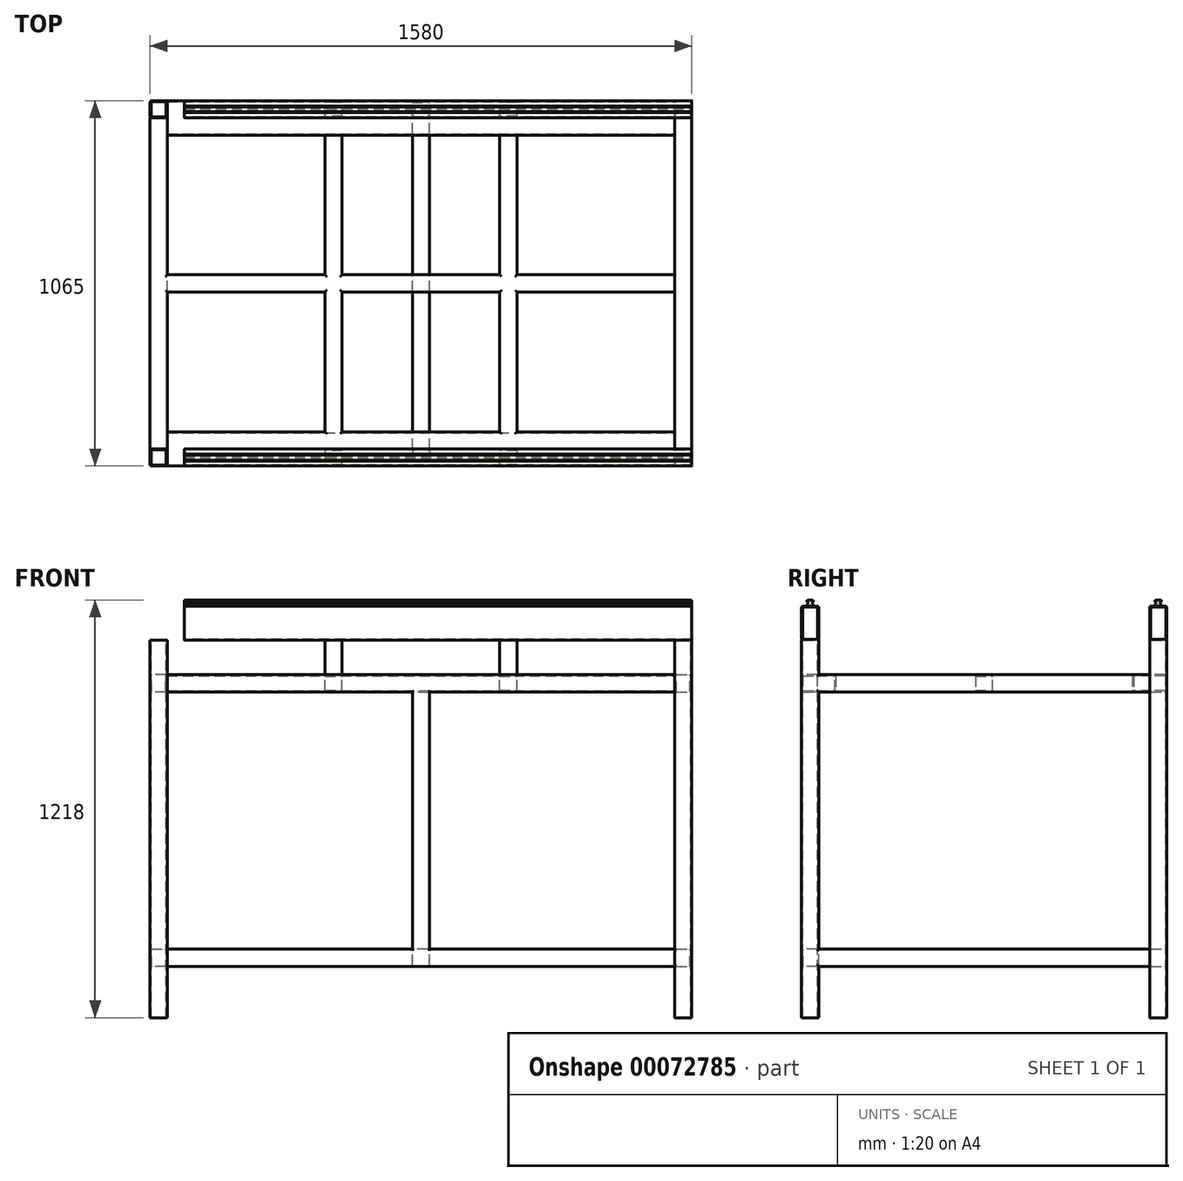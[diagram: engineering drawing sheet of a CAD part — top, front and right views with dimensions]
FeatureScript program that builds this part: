
annotation { "Feature Type Name" : "Feature", "Feature Type Description" : "" }
export const myFeature = defineFeature(function(context is Context, id is Id, definition is map)
    precondition{}
    {
        {
            var Q0;
            Q0=qCreatedBy(makeId("Right.planeOp"),FACE);
            var sketch = newSketch(context, id + "F0", { "sketchPlane" : qUnion([Q0])});
            skLineSegment(sketch, "E0.rect.bottom", {"start": v(20, 50) * mm, "end": v(-20, 50) * mm});
            skLineSegment(sketch, "E0.rect.top", {"start": v(20, -50) * mm, "end": v(-20, -50) * mm});
            skLineSegment(sketch, "E0.rect.left", {"start": v(25, 45) * mm, "end": v(25, -45) * mm});
            skLineSegment(sketch, "E0.rect.right", {"start": v(-25, 45) * mm, "end": v(-25, -45) * mm});
            skPoint(sketch, "E0.rect.middle", {"position": v(0, 0) * mm});
            skPoint(sketch, "E1.visualSharp", {"position": v(-25, 50) * mm});
            skArc(sketch, "E1.filletArc", {"start": v(-20, 50) * mm, "mid": v(-23.54, 48.54) * mm, "end": v(-25, 45) * mm});
            skPoint(sketch, "E2.visualSharp", {"position": v(25, 50) * mm});
            skArc(sketch, "E2.filletArc", {"start": v(25, 45) * mm, "mid": v(23.54, 48.54) * mm, "end": v(20, 50) * mm});
            skPoint(sketch, "E3.visualSharp", {"position": v(25, -50) * mm});
            skArc(sketch, "E3.filletArc", {"start": v(20, -50) * mm, "mid": v(23.54, -48.54) * mm, "end": v(25, -45) * mm});
            skPoint(sketch, "E4.visualSharp", {"position": v(-25, -50) * mm});
            skArc(sketch, "E4.filletArc", {"start": v(-25, -45) * mm, "mid": v(-23.54, -48.54) * mm, "end": v(-20, -50) * mm});
            skLineSegment(sketch, "E5.0", {"start": v(-22, 47) * mm, "end": v(-22, -47) * mm});
            skLineSegment(sketch, "E5.1", {"start": v(22, 47) * mm, "end": v(-22, 47) * mm});
            skLineSegment(sketch, "E5.2", {"start": v(22, 47) * mm, "end": v(22, -47) * mm});
            skLineSegment(sketch, "E5.3", {"start": v(22, -47) * mm, "end": v(-22, -47) * mm});
            skSolve(sketch);
        }
        {
            var Q0;
            Q0=qCreatedBy(makeId("Right.planeOp"),FACE);
            var sketch = newSketch(context, id + "F1", { "sketchPlane" : qUnion([Q0])});
            skLineSegment(sketch, "E6.rect.bottom", {"start": v(-995, 50) * mm, "end": v(-1035, 50) * mm});
            skLineSegment(sketch, "E6.rect.top", {"start": v(-995, -50) * mm, "end": v(-1035, -50) * mm});
            skLineSegment(sketch, "E6.rect.left", {"start": v(-990, 45) * mm, "end": v(-990, -45) * mm});
            skLineSegment(sketch, "E6.rect.right", {"start": v(-1040, 45) * mm, "end": v(-1040, -45) * mm});
            skPoint(sketch, "E6.rect.middle", {"position": v(0, 0) * mm});
            skPoint(sketch, "E7.visualSharp", {"position": v(-1040, 50) * mm});
            skArc(sketch, "E7.filletArc", {"start": v(-1035, 50) * mm, "mid": v(-1038.54, 48.54) * mm, "end": v(-1040, 45) * mm});
            skPoint(sketch, "E8.visualSharp", {"position": v(-990, 50) * mm});
            skArc(sketch, "E8.filletArc", {"start": v(-990, 45) * mm, "mid": v(-991.46, 48.54) * mm, "end": v(-995, 50) * mm});
            skPoint(sketch, "E9.visualSharp", {"position": v(-990, -50) * mm});
            skArc(sketch, "E9.filletArc", {"start": v(-995, -50) * mm, "mid": v(-991.46, -48.54) * mm, "end": v(-990, -45) * mm});
            skPoint(sketch, "E10.visualSharp", {"position": v(-1040, -50) * mm});
            skArc(sketch, "E10.filletArc", {"start": v(-1040, -45) * mm, "mid": v(-1038.54, -48.54) * mm, "end": v(-1035, -50) * mm});
            skLineSegment(sketch, "E11.0", {"start": v(-1037, 47) * mm, "end": v(-1037, -47) * mm});
            skLineSegment(sketch, "E11.1", {"start": v(-993, 47) * mm, "end": v(-1037, 47) * mm});
            skLineSegment(sketch, "E11.2", {"start": v(-993, 47) * mm, "end": v(-993, -47) * mm});
            skLineSegment(sketch, "E11.3", {"start": v(-993, -47) * mm, "end": v(-1037, -47) * mm});
            skSolve(sketch);
        }
        {
            var Q0;
            Q0=makeQuery(id+"F1.imprint","IMPRINT",FACE,{"disambiguationData":[TD([[makeQuery(id+"F1.imprint","IMPRINT",EDGE,{"derivedFrom":sQuery(id+"F1.wireOp",EDGE,"E6.rect.bottom")}),1.0]])]});
            var Q1;
            Q1=makeQuery(id+"F0.imprint","IMPRINT",FACE,{"disambiguationData":[TD([[makeQuery(id+"F0.imprint","IMPRINT",EDGE,{"derivedFrom":sQuery(id+"F0.wireOp",EDGE,"E0.rect.bottom")}),1.0]])]});
            extrude(context, id + "F2", {"entities" : qUnion([Q0, Q1]), "depth" : 1480 * mm});
        }
        {
            var Q0;
            Q0=makeQuery(id+"F2.opExtrude","CAP_FACE",FACE,{"disambiguationData":[OSD([sQuery(id+"F1.wireOp",EDGE,"E6.rect.bottom"),sQuery(id+"F1.wireOp",EDGE,"E6.rect.top"),sQuery(id+"F1.wireOp",EDGE,"E6.rect.left"),sQuery(id+"F1.wireOp",EDGE,"E6.rect.right"),sQuery(id+"F1.wireOp",EDGE,"E7.filletArc"),sQuery(id+"F1.wireOp",EDGE,"E8.filletArc"),sQuery(id+"F1.wireOp",EDGE,"E9.filletArc"),sQuery(id+"F1.wireOp",EDGE,"E10.filletArc"),sQuery(id+"F1.wireOp",EDGE,"E11.0"),sQuery(id+"F1.wireOp",EDGE,"E11.1"),sQuery(id+"F1.wireOp",EDGE,"E11.2"),sQuery(id+"F1.wireOp",EDGE,"E11.3")])],"isStart":false});
            cPlane(context, id + "F3", {"entities" : qUnion([Q0]), "cplaneType" : CPlaneType.OFFSET, "offset" : 50 * mm, "oppositeDirection" : true, "width" : 150 * mm, "height" : 150 * mm});
        }
        {
            var Q0;
            Q0=qCreatedBy(id+"F3.planeOp",FACE);
            var sketch = newSketch(context, id + "F4", { "sketchPlane" : qUnion([Q0])});
            skLineSegment(sketch, "E12.bottom", {"start": v(-1035, -150) * mm, "end": v(-945, -150) * mm});
            skLineSegment(sketch, "E12.top", {"start": v(-1035, -200) * mm, "end": v(-945, -200) * mm});
            skLineSegment(sketch, "E12.left", {"start": v(-1040, -155) * mm, "end": v(-1040, -195) * mm});
            skLineSegment(sketch, "E12.right", {"start": v(-940, -155) * mm, "end": v(-940, -195) * mm});
            skPoint(sketch, "E13.visualSharp", {"position": v(-1040, -150) * mm});
            skArc(sketch, "E13.filletArc", {"start": v(-1035, -150) * mm, "mid": v(-1038.54, -151.46) * mm, "end": v(-1040, -155) * mm});
            skPoint(sketch, "E14.visualSharp", {"position": v(-940, -150) * mm});
            skArc(sketch, "E14.filletArc", {"start": v(-940, -155) * mm, "mid": v(-941.46, -151.46) * mm, "end": v(-945, -150) * mm});
            skPoint(sketch, "E15.visualSharp", {"position": v(-940, -200) * mm});
            skArc(sketch, "E15.filletArc", {"start": v(-945, -200) * mm, "mid": v(-941.46, -198.54) * mm, "end": v(-940, -195) * mm});
            skPoint(sketch, "E16.visualSharp", {"position": v(-1040, -200) * mm});
            skArc(sketch, "E16.filletArc", {"start": v(-1040, -195) * mm, "mid": v(-1038.54, -198.54) * mm, "end": v(-1035, -200) * mm});
            skLineSegment(sketch, "E17.0", {"start": v(-995, -50) * mm, "end": v(-1035, -50) * mm});
            skLineSegment(sketch, "E18.0", {"start": v(-1040, 45) * mm, "end": v(-1040, -45) * mm});
            skLineSegment(sketch, "E19.0", {"start": v(-943, -153) * mm, "end": v(-943, -197) * mm});
            skLineSegment(sketch, "E19.1", {"start": v(-1037, -153) * mm, "end": v(-943, -153) * mm});
            skLineSegment(sketch, "E19.2", {"start": v(-1037, -153) * mm, "end": v(-1037, -197) * mm});
            skLineSegment(sketch, "E19.3", {"start": v(-1037, -197) * mm, "end": v(-943, -197) * mm});
            skLineSegment(sketch, "E20.bottom", {"start": v(20, -150) * mm, "end": v(-70, -150) * mm});
            skLineSegment(sketch, "E20.top", {"start": v(20, -200) * mm, "end": v(-70, -200) * mm});
            skLineSegment(sketch, "E20.left", {"start": v(25, -155) * mm, "end": v(25, -195) * mm});
            skLineSegment(sketch, "E20.right", {"start": v(-75, -155) * mm, "end": v(-75, -195) * mm});
            skPoint(sketch, "E21.0", {"position": v(25, -50) * mm});
            skPoint(sketch, "E22.visualSharp", {"position": v(-75, -150) * mm});
            skArc(sketch, "E22.filletArc", {"start": v(-70, -150) * mm, "mid": v(-73.54, -151.46) * mm, "end": v(-75, -155) * mm});
            skPoint(sketch, "E23.visualSharp", {"position": v(25, -200) * mm});
            skArc(sketch, "E23.filletArc", {"start": v(20, -200) * mm, "mid": v(23.54, -198.54) * mm, "end": v(25, -195) * mm});
            skPoint(sketch, "E24.visualSharp", {"position": v(25, -150) * mm});
            skArc(sketch, "E24.filletArc", {"start": v(25, -155) * mm, "mid": v(23.54, -151.46) * mm, "end": v(20, -150) * mm});
            skPoint(sketch, "E25.visualSharp", {"position": v(-75, -200) * mm});
            skArc(sketch, "E25.filletArc", {"start": v(-75, -195) * mm, "mid": v(-73.54, -198.54) * mm, "end": v(-70, -200) * mm});
            skLineSegment(sketch, "E26.0", {"start": v(22, -153) * mm, "end": v(-72, -153) * mm});
            skLineSegment(sketch, "E26.1", {"start": v(22, -153) * mm, "end": v(22, -197) * mm});
            skLineSegment(sketch, "E26.2", {"start": v(22, -197) * mm, "end": v(-72, -197) * mm});
            skLineSegment(sketch, "E26.3", {"start": v(-72, -153) * mm, "end": v(-72, -197) * mm});
            skSolve(sketch);
        }
        {
            var Q0;
            Q0=makeQuery(id+"F4.imprint","IMPRINT",FACE,{"disambiguationData":[TD([[makeQuery(id+"F4.imprint","IMPRINT",EDGE,{"derivedFrom":sQuery(id+"F4.wireOp",EDGE,"E12.bottom")}),-1.0]])]});
            var Q1;
            Q1=makeQuery(id+"F4.imprint","IMPRINT",FACE,{"disambiguationData":[TD([[makeQuery(id+"F4.imprint","IMPRINT",EDGE,{"derivedFrom":sQuery(id+"F4.wireOp",EDGE,"E20.bottom")}),1.0]])]});
            extrude(context, id + "F5", {"entities" : qUnion([Q0, Q1]), "oppositeDirection" : true, "depth" : 1480 * mm});
        }
        {
            var Q0;
            Q0=makeQuery(id+"F2.opExtrude","SWEPT_FACE",FACE,{"disambiguationData":[OSD([sQuery(id+"F1.wireOp",EDGE,"E6.rect.top")])]});
            cPlane(context, id + "F6", {"entities" : qUnion([Q0]), "cplaneType" : CPlaneType.OFFSET, "offset" : 0 * mm, "width" : 150 * mm, "height" : 150 * mm});
        }
        {
            var Q0;
            Q0=qCreatedBy(id+"F6.planeOp",FACE);
            var sketch = newSketch(context, id + "F7", { "sketchPlane" : qUnion([Q0])});
            skPoint(sketch, "E27.0", {"position": v(1480, 990) * mm});
            skPoint(sketch, "E28.0", {"position": v(1430, 1040) * mm});
            skLineSegment(sketch, "E29.bottom", {"start": v(1435, 1040) * mm, "end": v(1475, 1040) * mm});
            skLineSegment(sketch, "E29.top", {"start": v(1435, 990) * mm, "end": v(1475, 990) * mm});
            skLineSegment(sketch, "E29.left", {"start": v(1430, 1035) * mm, "end": v(1430, 995) * mm});
            skLineSegment(sketch, "E29.right", {"start": v(1480, 1035) * mm, "end": v(1480, 995) * mm});
            skPoint(sketch, "E30.visualSharp", {"position": v(1480, 1040) * mm});
            skArc(sketch, "E30.filletArc", {"start": v(1480, 1035) * mm, "mid": v(1478.54, 1038.54) * mm, "end": v(1475, 1040) * mm});
            skArc(sketch, "E31.filletArc", {"start": v(1475, 990) * mm, "mid": v(1478.54, 991.46) * mm, "end": v(1480, 995) * mm});
            skPoint(sketch, "E32.visualSharp", {"position": v(1430, 990) * mm});
            skArc(sketch, "E32.filletArc", {"start": v(1430, 995) * mm, "mid": v(1431.46, 991.46) * mm, "end": v(1435, 990) * mm});
            skArc(sketch, "E33.filletArc", {"start": v(1435, 1040) * mm, "mid": v(1431.46, 1038.54) * mm, "end": v(1430, 1035) * mm});
            skLineSegment(sketch, "E34.0", {"start": v(1477, 1037) * mm, "end": v(1477, 993) * mm});
            skLineSegment(sketch, "E34.1", {"start": v(1433, 1037) * mm, "end": v(1477, 1037) * mm});
            skLineSegment(sketch, "E34.2", {"start": v(1433, 1037) * mm, "end": v(1433, 993) * mm});
            skLineSegment(sketch, "E34.3", {"start": v(1433, 993) * mm, "end": v(1477, 993) * mm});
            skSolve(sketch);
        }
        {
            var Q0;
            Q0=makeQuery(id+"F7.imprint","IMPRINT",FACE,{"disambiguationData":[TD([[makeQuery(id+"F7.imprint","IMPRINT",EDGE,{"derivedFrom":sQuery(id+"F7.wireOp",EDGE,"E29.bottom")}),-1.0]])]});
            extrude(context, id + "F8", {"entities" : qUnion([Q0]), "operationType" : NewBodyOperationType.ADD, "depth" : 1100 * mm});
        }
        {
            var Q0;
            Q0=qCreatedBy(id+"F6.planeOp",FACE);
            var sketch = newSketch(context, id + "F9", { "sketchPlane" : qUnion([Q0])});
            skPoint(sketch, "E35.0", {"position": v(1480, -25) * mm});
            skPoint(sketch, "E36.0", {"position": v(1480, 25) * mm});
            skPoint(sketch, "E37.0", {"position": v(1430, -25) * mm});
            skLineSegment(sketch, "E38.bottom", {"start": v(1475, 25) * mm, "end": v(1435, 25) * mm});
            skLineSegment(sketch, "E38.top", {"start": v(1475, -25) * mm, "end": v(1435, -25) * mm});
            skLineSegment(sketch, "E38.left", {"start": v(1480, 20) * mm, "end": v(1480, -20) * mm});
            skLineSegment(sketch, "E38.right", {"start": v(1430, 20) * mm, "end": v(1430, -20) * mm});
            skArc(sketch, "E39.filletArc", {"start": v(1480, 20) * mm, "mid": v(1478.54, 23.54) * mm, "end": v(1475, 25) * mm});
            skPoint(sketch, "E40.visualSharp", {"position": v(1430, 25) * mm});
            skArc(sketch, "E40.filletArc", {"start": v(1435, 25) * mm, "mid": v(1431.46, 23.54) * mm, "end": v(1430, 20) * mm});
            skArc(sketch, "E41.filletArc", {"start": v(1430, -20) * mm, "mid": v(1431.46, -23.54) * mm, "end": v(1435, -25) * mm});
            skArc(sketch, "E42.filletArc", {"start": v(1475, -25) * mm, "mid": v(1478.54, -23.54) * mm, "end": v(1480, -20) * mm});
            skLineSegment(sketch, "E43.0", {"start": v(1477, 22) * mm, "end": v(1433, 22) * mm});
            skLineSegment(sketch, "E43.1", {"start": v(1477, 22) * mm, "end": v(1477, -22) * mm});
            skLineSegment(sketch, "E43.2", {"start": v(1477, -22) * mm, "end": v(1433, -22) * mm});
            skLineSegment(sketch, "E43.3", {"start": v(1433, 22) * mm, "end": v(1433, -22) * mm});
            skSolve(sketch);
        }
        {
            var Q0;
            Q0=makeQuery(id+"F9.imprint","IMPRINT",FACE,{"disambiguationData":[TD([[makeQuery(id+"F9.imprint","IMPRINT",EDGE,{"derivedFrom":sQuery(id+"F9.wireOp",EDGE,"E38.bottom")}),1.0]])]});
            extrude(context, id + "F10", {"entities" : qUnion([Q0]), "operationType" : NewBodyOperationType.ADD, "depth" : 1100 * mm});
        }
        {
            var Q0;
            Q0=qCreatedBy(id+"F6.planeOp",FACE);
            var sketch = newSketch(context, id + "F11", { "sketchPlane" : qUnion([Q0])});
            skPoint(sketch, "E44.0", {"position": v(-50, 1040) * mm});
            skLineSegment(sketch, "E45.bottom", {"start": v(-55, 1040) * mm, "end": v(-95, 1040) * mm});
            skLineSegment(sketch, "E45.top", {"start": v(-55, 990) * mm, "end": v(-95, 990) * mm});
            skLineSegment(sketch, "E45.left", {"start": v(-50, 1035) * mm, "end": v(-50, 995) * mm});
            skLineSegment(sketch, "E45.right", {"start": v(-100, 1035) * mm, "end": v(-100, 995) * mm});
            skPoint(sketch, "E46.visualSharp", {"position": v(-100, 1040) * mm});
            skArc(sketch, "E46.filletArc", {"start": v(-95, 1040) * mm, "mid": v(-98.54, 1038.54) * mm, "end": v(-100, 1035) * mm});
            skArc(sketch, "E47.filletArc", {"start": v(-50, 1035) * mm, "mid": v(-51.46, 1038.54) * mm, "end": v(-55, 1040) * mm});
            skPoint(sketch, "E48.visualSharp", {"position": v(-50, 990) * mm});
            skArc(sketch, "E48.filletArc", {"start": v(-55, 990) * mm, "mid": v(-51.46, 991.46) * mm, "end": v(-50, 995) * mm});
            skPoint(sketch, "E49.visualSharp", {"position": v(-100, 990) * mm});
            skArc(sketch, "E49.filletArc", {"start": v(-100, 995) * mm, "mid": v(-98.54, 991.46) * mm, "end": v(-95, 990) * mm});
            skLineSegment(sketch, "E50.0", {"start": v(-53, 1037) * mm, "end": v(-97, 1037) * mm});
            skLineSegment(sketch, "E50.1", {"start": v(-53, 1037) * mm, "end": v(-53, 993) * mm});
            skLineSegment(sketch, "E50.2", {"start": v(-53, 993) * mm, "end": v(-97, 993) * mm});
            skLineSegment(sketch, "E50.3", {"start": v(-97, 1037) * mm, "end": v(-97, 993) * mm});
            skSolve(sketch);
        }
        {
            var Q0;
            Q0=makeQuery(id+"F11.imprint","IMPRINT",FACE,{"disambiguationData":[TD([[makeQuery(id+"F11.imprint","IMPRINT",EDGE,{"derivedFrom":sQuery(id+"F11.wireOp",EDGE,"E45.bottom")}),1.0]])]});
            extrude(context, id + "F12", {"entities" : qUnion([Q0]), "operationType" : NewBodyOperationType.ADD, "depth" : 1100 * mm});
        }
        {
            var Q0;
            Q0=qCreatedBy(id+"F6.planeOp",FACE);
            var sketch = newSketch(context, id + "F13", { "sketchPlane" : qUnion([Q0])});
            skPoint(sketch, "E51.0", {"position": v(-50, -25) * mm});
            skLineSegment(sketch, "E52.bottom", {"start": v(-55, -25) * mm, "end": v(-95, -25) * mm});
            skLineSegment(sketch, "E52.top", {"start": v(-55, 25) * mm, "end": v(-95, 25) * mm});
            skLineSegment(sketch, "E52.left", {"start": v(-50, -20) * mm, "end": v(-50, 20) * mm});
            skLineSegment(sketch, "E52.right", {"start": v(-100, -20) * mm, "end": v(-100, 20) * mm});
            skPoint(sketch, "E53.visualSharp", {"position": v(-100, 25) * mm});
            skArc(sketch, "E53.filletArc", {"start": v(-95, 25) * mm, "mid": v(-98.54, 23.54) * mm, "end": v(-100, 20) * mm});
            skPoint(sketch, "E54.visualSharp", {"position": v(-100, -25) * mm});
            skArc(sketch, "E54.filletArc", {"start": v(-100, -20) * mm, "mid": v(-98.54, -23.54) * mm, "end": v(-95, -25) * mm});
            skArc(sketch, "E55.filletArc", {"start": v(-55, -25) * mm, "mid": v(-51.46, -23.54) * mm, "end": v(-50, -20) * mm});
            skPoint(sketch, "E56.visualSharp", {"position": v(-50, 25) * mm});
            skArc(sketch, "E56.filletArc", {"start": v(-50, 20) * mm, "mid": v(-51.46, 23.54) * mm, "end": v(-55, 25) * mm});
            skLineSegment(sketch, "E57.0", {"start": v(-53, 22) * mm, "end": v(-97, 22) * mm});
            skLineSegment(sketch, "E57.1", {"start": v(-53, -22) * mm, "end": v(-53, 22) * mm});
            skLineSegment(sketch, "E57.2", {"start": v(-53, -22) * mm, "end": v(-97, -22) * mm});
            skLineSegment(sketch, "E57.3", {"start": v(-97, -22) * mm, "end": v(-97, 22) * mm});
            skSolve(sketch);
        }
        {
            var Q0;
            Q0=makeQuery(id+"F13.imprint","IMPRINT",FACE,{"disambiguationData":[TD([[makeQuery(id+"F13.imprint","IMPRINT",EDGE,{"derivedFrom":sQuery(id+"F13.wireOp",EDGE,"E52.bottom")}),-1.0]])]});
            extrude(context, id + "F14", {"entities" : qUnion([Q0]), "operationType" : NewBodyOperationType.ADD, "depth" : 1100 * mm});
        }
        {
            var Q0;
            Q0=makeQuery(id+"F10.opExtrude","SWEPT_FACE",FACE,{"disambiguationData":[OSD([sQuery(id+"F9.wireOp",EDGE,"E38.bottom")])]});
            cPlane(context, id + "F15", {"entities" : qUnion([Q0]), "cplaneType" : CPlaneType.OFFSET, "offset" : 0 * mm, "width" : 150 * mm, "height" : 150 * mm});
        }
        {
            var Q0;
            Q0=qCreatedBy(id+"F15.planeOp",FACE);
            var sketch = newSketch(context, id + "F16", { "sketchPlane" : qUnion([Q0])});
            skPoint(sketch, "E58.0", {"position": v(1430, -150) * mm});
            skLineSegment(sketch, "E59.bottom", {"start": v(1435, -150) * mm, "end": v(1475, -150) * mm});
            skLineSegment(sketch, "E59.top", {"start": v(1435, -200) * mm, "end": v(1475, -200) * mm});
            skLineSegment(sketch, "E59.left", {"start": v(1430, -155) * mm, "end": v(1430, -195) * mm});
            skLineSegment(sketch, "E59.right", {"start": v(1480, -155) * mm, "end": v(1480, -195) * mm});
            skPoint(sketch, "E60.0", {"position": v(1430, -200) * mm});
            skArc(sketch, "E61.filletArc", {"start": v(1435, -150) * mm, "mid": v(1431.46, -151.46) * mm, "end": v(1430, -155) * mm});
            skArc(sketch, "E62.filletArc", {"start": v(1430, -195) * mm, "mid": v(1431.46, -198.54) * mm, "end": v(1435, -200) * mm});
            skPoint(sketch, "E63.visualSharp", {"position": v(1480, -200) * mm});
            skArc(sketch, "E63.filletArc", {"start": v(1475, -200) * mm, "mid": v(1478.54, -198.54) * mm, "end": v(1480, -195) * mm});
            skPoint(sketch, "E64.visualSharp", {"position": v(1480, -150) * mm});
            skArc(sketch, "E64.filletArc", {"start": v(1480, -155) * mm, "mid": v(1478.54, -151.46) * mm, "end": v(1475, -150) * mm});
            skSolve(sketch);
        }
        {
            var Q0;
            Q0=makeQuery(id+"F16.imprint","IMPRINT",FACE,{"disambiguationData":[TD([[makeQuery(id+"F16.imprint","IMPRINT",EDGE,{"derivedFrom":sQuery(id+"F16.wireOp",EDGE,"E59.bottom")}),-1.0]])]});
            extrude(context, id + "F17", {"entities" : qUnion([Q0]), "operationType" : NewBodyOperationType.ADD, "endBound" : BoundingType.UP_TO_NEXT, "depth" : 965 * mm});
        }
        {
            var Q0;
            Q0=qCreatedBy(id+"F15.planeOp",FACE);
            var sketch = newSketch(context, id + "F18", { "sketchPlane" : qUnion([Q0])});
            skPoint(sketch, "E65.0", {"position": v(-50, -150) * mm});
            skPoint(sketch, "E66.0", {"position": v(-50, -200) * mm});
            skLineSegment(sketch, "E67.bottom", {"start": v(-55, -150) * mm, "end": v(-95, -150) * mm});
            skLineSegment(sketch, "E67.top", {"start": v(-55, -200) * mm, "end": v(-95, -200) * mm});
            skLineSegment(sketch, "E67.left", {"start": v(-50, -155) * mm, "end": v(-50, -195) * mm});
            skLineSegment(sketch, "E67.right", {"start": v(-100, -155) * mm, "end": v(-100, -195) * mm});
            skPoint(sketch, "E68.visualSharp", {"position": v(-100, -150) * mm});
            skArc(sketch, "E68.filletArc", {"start": v(-95, -150) * mm, "mid": v(-98.54, -151.46) * mm, "end": v(-100, -155) * mm});
            skPoint(sketch, "E69.visualSharp", {"position": v(-100, -200) * mm});
            skArc(sketch, "E69.filletArc", {"start": v(-100, -195) * mm, "mid": v(-98.54, -198.54) * mm, "end": v(-95, -200) * mm});
            skArc(sketch, "E70.filletArc", {"start": v(-55, -200) * mm, "mid": v(-51.46, -198.54) * mm, "end": v(-50, -195) * mm});
            skArc(sketch, "E71.filletArc", {"start": v(-50, -155) * mm, "mid": v(-51.46, -151.46) * mm, "end": v(-55, -150) * mm});
            skSolve(sketch);
        }
        {
            var Q0;
            Q0=makeQuery(id+"F18.imprint","IMPRINT",FACE,{"disambiguationData":[TD([[makeQuery(id+"F18.imprint","IMPRINT",EDGE,{"derivedFrom":sQuery(id+"F18.wireOp",EDGE,"E67.bottom")}),1.0]])]});
            extrude(context, id + "F19", {"entities" : qUnion([Q0]), "operationType" : NewBodyOperationType.ADD, "endBound" : BoundingType.UP_TO_NEXT, "depth" : 965 * mm});
        }
        {
            var Q0;
            Q0=qCreatedBy(id+"F15.planeOp",FACE);
            var sketch = newSketch(context, id + "F20", { "sketchPlane" : qUnion([Q0])});
            skPoint(sketch, "E72.0", {"position": v(1480, -1150) * mm});
            skPoint(sketch, "E73.0", {"position": v(1430, -1150) * mm});
            skLineSegment(sketch, "E74.bottom", {"start": v(1430, -1150) * mm, "end": v(1480, -1150) * mm, "construction": true});
            skLineSegment(sketch, "E74.top", {"start": v(1430, -1000) * mm, "end": v(1480, -1000) * mm, "construction": true});
            skLineSegment(sketch, "E74.left", {"start": v(1430, -1150) * mm, "end": v(1430, -1000) * mm, "construction": true});
            skLineSegment(sketch, "E74.right", {"start": v(1480, -1150) * mm, "end": v(1480, -1000) * mm, "construction": true});
            skLineSegment(sketch, "E75.bottom", {"start": v(1435, -1000) * mm, "end": v(1475, -1000) * mm});
            skLineSegment(sketch, "E75.top", {"start": v(1435, -950) * mm, "end": v(1475, -950) * mm});
            skLineSegment(sketch, "E75.left", {"start": v(1430, -995) * mm, "end": v(1430, -955) * mm});
            skLineSegment(sketch, "E75.right", {"start": v(1480, -995) * mm, "end": v(1480, -955) * mm});
            skPoint(sketch, "E76.visualSharp", {"position": v(1480, -950) * mm});
            skArc(sketch, "E76.filletArc", {"start": v(1480, -955) * mm, "mid": v(1478.54, -951.46) * mm, "end": v(1475, -950) * mm});
            skPoint(sketch, "E77.visualSharp", {"position": v(1480, -1000) * mm});
            skArc(sketch, "E77.filletArc", {"start": v(1475, -1000) * mm, "mid": v(1478.54, -998.54) * mm, "end": v(1480, -995) * mm});
            skPoint(sketch, "E78.visualSharp", {"position": v(1430, -1000) * mm});
            skArc(sketch, "E78.filletArc", {"start": v(1430, -995) * mm, "mid": v(1431.46, -998.54) * mm, "end": v(1435, -1000) * mm});
            skPoint(sketch, "E79.visualSharp", {"position": v(1430, -950) * mm});
            skArc(sketch, "E79.filletArc", {"start": v(1435, -950) * mm, "mid": v(1431.46, -951.46) * mm, "end": v(1430, -955) * mm});
            skSolve(sketch);
        }
        {
            var Q0;
            Q0=makeQuery(id+"F20.imprint","IMPRINT",FACE,{"disambiguationData":[TD([[makeQuery(id+"F20.imprint","IMPRINT",EDGE,{"derivedFrom":sQuery(id+"F20.wireOp",EDGE,"E75.bottom")}),1.0]])]});
            extrude(context, id + "F21", {"entities" : qUnion([Q0]), "operationType" : NewBodyOperationType.ADD, "endBound" : BoundingType.UP_TO_NEXT, "depth" : 965 * mm});
        }
        {
            var Q0;
            Q0=qCreatedBy(id+"F15.planeOp",FACE);
            var sketch = newSketch(context, id + "F22", { "sketchPlane" : qUnion([Q0])});
            skPoint(sketch, "E80.0", {"position": v(-50, -1150) * mm});
            skPoint(sketch, "E81.0", {"position": v(-100, -1150) * mm});
            skLineSegment(sketch, "E82.bottom", {"start": v(-100, -1150) * mm, "end": v(-50, -1150) * mm, "construction": true});
            skLineSegment(sketch, "E82.top", {"start": v(-100, -1000) * mm, "end": v(-50, -1000) * mm, "construction": true});
            skLineSegment(sketch, "E82.left", {"start": v(-100, -1150) * mm, "end": v(-100, -1000) * mm, "construction": true});
            skLineSegment(sketch, "E82.right", {"start": v(-50, -1150) * mm, "end": v(-50, -1000) * mm, "construction": true});
            skLineSegment(sketch, "E83.bottom", {"start": v(-95, -1000) * mm, "end": v(-55, -1000) * mm});
            skLineSegment(sketch, "E83.top", {"start": v(-95, -950) * mm, "end": v(-55, -950) * mm});
            skLineSegment(sketch, "E83.left", {"start": v(-100, -995) * mm, "end": v(-100, -955) * mm});
            skLineSegment(sketch, "E83.right", {"start": v(-50, -995) * mm, "end": v(-50, -955) * mm});
            skPoint(sketch, "E84.visualSharp", {"position": v(-50, -950) * mm});
            skArc(sketch, "E84.filletArc", {"start": v(-50, -955) * mm, "mid": v(-51.46, -951.46) * mm, "end": v(-55, -950) * mm});
            skPoint(sketch, "E85.visualSharp", {"position": v(-100, -950) * mm});
            skArc(sketch, "E85.filletArc", {"start": v(-95, -950) * mm, "mid": v(-98.54, -951.46) * mm, "end": v(-100, -955) * mm});
            skPoint(sketch, "E86.visualSharp", {"position": v(-100, -1000) * mm});
            skArc(sketch, "E86.filletArc", {"start": v(-100, -995) * mm, "mid": v(-98.54, -998.54) * mm, "end": v(-95, -1000) * mm});
            skPoint(sketch, "E87.visualSharp", {"position": v(-50, -1000) * mm});
            skArc(sketch, "E87.filletArc", {"start": v(-55, -1000) * mm, "mid": v(-51.46, -998.54) * mm, "end": v(-50, -995) * mm});
            skSolve(sketch);
        }
        {
            var Q0;
            Q0=makeQuery(id+"F22.imprint","IMPRINT",FACE,{"disambiguationData":[TD([[makeQuery(id+"F22.imprint","IMPRINT",EDGE,{"derivedFrom":sQuery(id+"F22.wireOp",EDGE,"E83.bottom")}),1.0]])]});
            extrude(context, id + "F23", {"entities" : qUnion([Q0]), "operationType" : NewBodyOperationType.ADD, "endBound" : BoundingType.UP_TO_NEXT, "depth" : 965 * mm});
        }
        {
            var Q0;
            Q0=makeQuery(id+"F5.opExtrude","SWEPT_FACE",FACE,{"disambiguationData":[OSD([sQuery(id+"F4.wireOp",EDGE,"E20.right")])]});
            cPlane(context, id + "F24", {"entities" : qUnion([Q0]), "cplaneType" : CPlaneType.OFFSET, "offset" : 0 * mm, "width" : 150 * mm, "height" : 150 * mm});
        }
        {
            var Q0;
            Q0=qCreatedBy(id+"F24.planeOp",FACE);
            var sketch = newSketch(context, id + "F25", { "sketchPlane" : qUnion([Q0])});
            skPoint(sketch, "E88.0", {"position": v(-50, -150) * mm});
            skPoint(sketch, "E89.0", {"position": v(-50, -200) * mm});
            skLineSegment(sketch, "E90.bottom", {"start": v(-50, -150) * mm, "end": v(410, -150) * mm, "construction": true});
            skLineSegment(sketch, "E90.top", {"start": v(-50, -200) * mm, "end": v(410, -200) * mm, "construction": true});
            skLineSegment(sketch, "E90.left", {"start": v(-50, -150) * mm, "end": v(-50, -200) * mm, "construction": true});
            skLineSegment(sketch, "E90.right", {"start": v(410, -150) * mm, "end": v(410, -200) * mm, "construction": true});
            skLineSegment(sketch, "E91.bottom", {"start": v(415, -150) * mm, "end": v(455, -150) * mm});
            skLineSegment(sketch, "E91.top", {"start": v(415, -200) * mm, "end": v(455, -200) * mm});
            skLineSegment(sketch, "E91.left", {"start": v(410, -155) * mm, "end": v(410, -195) * mm});
            skLineSegment(sketch, "E91.right", {"start": v(460, -155) * mm, "end": v(460, -195) * mm});
            skLineSegment(sketch, "E92.bottom", {"start": v(460, -150) * mm, "end": v(920, -150) * mm, "construction": true});
            skLineSegment(sketch, "E92.top", {"start": v(460, -200) * mm, "end": v(920, -200) * mm, "construction": true});
            skLineSegment(sketch, "E92.left", {"start": v(460, -150) * mm, "end": v(460, -200) * mm, "construction": true});
            skLineSegment(sketch, "E92.right", {"start": v(920, -150) * mm, "end": v(920, -200) * mm, "construction": true});
            skLineSegment(sketch, "E93.bottom", {"start": v(925, -150) * mm, "end": v(965, -150) * mm});
            skLineSegment(sketch, "E93.top", {"start": v(925, -200) * mm, "end": v(965, -200) * mm});
            skLineSegment(sketch, "E93.left", {"start": v(920, -155) * mm, "end": v(920, -195) * mm});
            skLineSegment(sketch, "E93.right", {"start": v(970, -155) * mm, "end": v(970, -195) * mm});
            skPoint(sketch, "E94.0", {"position": v(1430, -200) * mm});
            skLineSegment(sketch, "E95.bottom", {"start": v(1430, -200) * mm, "end": v(970, -200) * mm, "construction": true});
            skLineSegment(sketch, "E95.top", {"start": v(1430, -150) * mm, "end": v(970, -150) * mm, "construction": true});
            skLineSegment(sketch, "E95.left", {"start": v(1430, -200) * mm, "end": v(1430, -150) * mm, "construction": true});
            skLineSegment(sketch, "E95.right", {"start": v(970, -200) * mm, "end": v(970, -150) * mm, "construction": true});
            skPoint(sketch, "E96.visualSharp", {"position": v(410, -150) * mm});
            skArc(sketch, "E96.filletArc", {"start": v(415, -150) * mm, "mid": v(411.46, -151.46) * mm, "end": v(410, -155) * mm});
            skPoint(sketch, "E97.visualSharp", {"position": v(460, -150) * mm});
            skArc(sketch, "E97.filletArc", {"start": v(460, -155) * mm, "mid": v(458.54, -151.46) * mm, "end": v(455, -150) * mm});
            skPoint(sketch, "E98.visualSharp", {"position": v(460, -200) * mm});
            skArc(sketch, "E98.filletArc", {"start": v(455, -200) * mm, "mid": v(458.54, -198.54) * mm, "end": v(460, -195) * mm});
            skPoint(sketch, "E99.visualSharp", {"position": v(410, -200) * mm});
            skArc(sketch, "E99.filletArc", {"start": v(410, -195) * mm, "mid": v(411.46, -198.54) * mm, "end": v(415, -200) * mm});
            skPoint(sketch, "E100.visualSharp", {"position": v(920, -150) * mm});
            skArc(sketch, "E100.filletArc", {"start": v(925, -150) * mm, "mid": v(921.46, -151.46) * mm, "end": v(920, -155) * mm});
            skPoint(sketch, "E101.visualSharp", {"position": v(970, -150) * mm});
            skArc(sketch, "E101.filletArc", {"start": v(970, -155) * mm, "mid": v(968.54, -151.46) * mm, "end": v(965, -150) * mm});
            skPoint(sketch, "E102.visualSharp", {"position": v(970, -200) * mm});
            skArc(sketch, "E102.filletArc", {"start": v(965, -200) * mm, "mid": v(968.54, -198.54) * mm, "end": v(970, -195) * mm});
            skPoint(sketch, "E103.visualSharp", {"position": v(920, -200) * mm});
            skArc(sketch, "E103.filletArc", {"start": v(920, -195) * mm, "mid": v(921.46, -198.54) * mm, "end": v(925, -200) * mm});
            skSolve(sketch);
        }
        {
            var Q0;
            Q0=makeQuery(id+"F25.imprint","IMPRINT",FACE,{"disambiguationData":[TD([[makeQuery(id+"F25.imprint","IMPRINT",EDGE,{"derivedFrom":sQuery(id+"F25.wireOp",EDGE,"E91.bottom")}),-1.0]])]});
            var Q1;
            Q1=makeQuery(id+"F25.imprint","IMPRINT",FACE,{"disambiguationData":[TD([[makeQuery(id+"F25.imprint","IMPRINT",EDGE,{"derivedFrom":sQuery(id+"F25.wireOp",EDGE,"E93.bottom")}),-1.0]])]});
            extrude(context, id + "F26", {"entities" : qUnion([Q0, Q1]), "operationType" : NewBodyOperationType.ADD, "endBound" : BoundingType.UP_TO_NEXT, "depth" : 865 * mm});
        }
        {
            var Q0;
            {var subQ0=sQuery(id+"F11.wireOp",EDGE,"E45.left");var subQ4=sQuery(id+"F4.wireOp",EDGE,"E12.top");Q0=makeQuery(id+"F23.boolean.opBoolean","MERGE",FACE,{"derivedFrom":[makeQuery(id+"F12.boolean.opBoolean","SPLIT",FACE,{"disambiguationData":[TD([makeQuery(id+"F5.opExtrude","SWEPT_FACE",FACE,{"disambiguationData":[OSD([subQ4])]})])],"derivedFrom":makeQuery(id+"F12.opExtrude","SWEPT_FACE",FACE,{"disambiguationData":[OSD([subQ0])]})}),makeQuery(id+"F23.opExtrude","SWEPT_FACE",FACE,{"disambiguationData":[OSD([sQuery(id+"F22.wireOp",EDGE,"E83.right")])]})]});}
            cPlane(context, id + "F27", {"entities" : qUnion([Q0]), "cplaneType" : CPlaneType.OFFSET, "offset" : 10 * mm, "width" : 150 * mm, "height" : 150 * mm});
        }
        {
            var Q0;
            Q0=qCreatedBy(id+"F27.planeOp",FACE);
            var sketch = newSketch(context, id + "F28", { "sketchPlane" : qUnion([Q0])});
            skPoint(sketch, "E104.0", {"position": v(-990, -1000) * mm});
            skPoint(sketch, "E105.0", {"position": v(-990, -950) * mm});
            skLineSegment(sketch, "E106.bottom", {"start": v(-995, -950) * mm, "end": v(-1035, -950) * mm});
            skLineSegment(sketch, "E106.top", {"start": v(-995, -1000) * mm, "end": v(-1035, -1000) * mm});
            skLineSegment(sketch, "E106.left", {"start": v(-990, -955) * mm, "end": v(-990, -995) * mm});
            skLineSegment(sketch, "E106.right", {"start": v(-1040, -955) * mm, "end": v(-1040, -995) * mm});
            skArc(sketch, "E107.filletArc", {"start": v(-990, -955) * mm, "mid": v(-991.46, -951.46) * mm, "end": v(-995, -950) * mm});
            skPoint(sketch, "E108.visualSharp", {"position": v(-1040, -950) * mm});
            skArc(sketch, "E108.filletArc", {"start": v(-1035, -950) * mm, "mid": v(-1038.54, -951.46) * mm, "end": v(-1040, -955) * mm});
            skPoint(sketch, "E109.visualSharp", {"position": v(-1040, -1000) * mm});
            skArc(sketch, "E109.filletArc", {"start": v(-1040, -995) * mm, "mid": v(-1038.54, -998.54) * mm, "end": v(-1035, -1000) * mm});
            skArc(sketch, "E110.filletArc", {"start": v(-995, -1000) * mm, "mid": v(-991.46, -998.54) * mm, "end": v(-990, -995) * mm});
            skSolve(sketch);
        }
        {
            var Q0;
            Q0=qSketchRegion(id+"F28",true);
            var Q1;
            Q1=makeQuery(id+"F8.opExtrude","SWEPT_FACE",FACE,{"disambiguationData":[OSD([sQuery(id+"F7.wireOp",EDGE,"E29.left")])]});
            var Q2;
            Q2=makeQuery(id+"F12.opExtrude","SWEPT_FACE",FACE,{"disambiguationData":[OSD([sQuery(id+"F11.wireOp",EDGE,"E45.left")])]});
            extrude(context, id + "F29", {"entities" : qUnion([Q0]), "operationType" : NewBodyOperationType.ADD, "endBound" : BoundingType.UP_TO_SURFACE, "endBoundEntityFace" : qUnion([Q1]), "depth" : 1530 * mm, "hasSecondDirection" : true, "secondDirectionBound" : SecondDirectionBoundingType.UP_TO_SURFACE, "secondDirectionOppositeDirection" : true, "secondDirectionBoundEntityFace" : qUnion([Q2]), "secondDirectionDepth" : 25 * mm});
        }
        {
            var Q0;
            Q0=qCreatedBy(id+"F27.planeOp",FACE);
            var sketch = newSketch(context, id + "F30", { "sketchPlane" : qUnion([Q0])});
            skPoint(sketch, "E111.0", {"position": v(-25, -1000) * mm});
            skPoint(sketch, "E112.0", {"position": v(-25, -950) * mm});
            skLineSegment(sketch, "E113.bottom", {"start": v(-20, -950) * mm, "end": v(20, -950) * mm});
            skLineSegment(sketch, "E113.top", {"start": v(-20, -1000) * mm, "end": v(20, -1000) * mm});
            skLineSegment(sketch, "E113.left", {"start": v(-25, -955) * mm, "end": v(-25, -995) * mm});
            skLineSegment(sketch, "E113.right", {"start": v(25, -955) * mm, "end": v(25, -995) * mm});
            skArc(sketch, "E114.filletArc", {"start": v(-20, -950) * mm, "mid": v(-23.54, -951.46) * mm, "end": v(-25, -955) * mm});
            skPoint(sketch, "E115.visualSharp", {"position": v(25, -950) * mm});
            skArc(sketch, "E115.filletArc", {"start": v(25, -955) * mm, "mid": v(23.54, -951.46) * mm, "end": v(20, -950) * mm});
            skPoint(sketch, "E116.visualSharp", {"position": v(25, -1000) * mm});
            skArc(sketch, "E116.filletArc", {"start": v(20, -1000) * mm, "mid": v(23.54, -998.54) * mm, "end": v(25, -995) * mm});
            skArc(sketch, "E117.filletArc", {"start": v(-25, -995) * mm, "mid": v(-23.54, -998.54) * mm, "end": v(-20, -1000) * mm});
            skSolve(sketch);
        }
        {
            var Q0;
            Q0=makeQuery(id+"F30.imprint","IMPRINT",FACE,{"disambiguationData":[TD([[makeQuery(id+"F30.imprint","IMPRINT",EDGE,{"derivedFrom":sQuery(id+"F30.wireOp",EDGE,"E113.bottom")}),-1.0]])]});
            var Q1;
            {var subQ0=sQuery(id+"F9.wireOp",EDGE,"E38.right");var subQ4=sQuery(id+"F4.wireOp",EDGE,"E20.top");Q1=makeQuery(id+"Fz8Vrk44a0iJE9b_11.opBoolean","SPLIT",FACE,{"disambiguationData":[TD([makeQuery(id+"F5.opExtrude","SWEPT_FACE",FACE,{"disambiguationData":[OSD([subQ4])]})])],"derivedFrom":makeQuery(id+"F10.opExtrude","SWEPT_FACE",FACE,{"disambiguationData":[OSD([subQ0])]})});}
            var Q2;
            {var subQ0=sQuery(id+"F13.wireOp",EDGE,"E52.left");var subQ4=sQuery(id+"F4.wireOp",EDGE,"E20.top");Q2=makeQuery(id+"Fz8Vrk44a0iJE9b_11.opBoolean","SPLIT",FACE,{"disambiguationData":[TD([makeQuery(id+"F5.opExtrude","SWEPT_FACE",FACE,{"disambiguationData":[OSD([subQ4])]})])],"derivedFrom":makeQuery(id+"F14.opExtrude","SWEPT_FACE",FACE,{"disambiguationData":[OSD([subQ0])]})});}
            extrude(context, id + "F31", {"entities" : qUnion([Q0]), "operationType" : NewBodyOperationType.ADD, "endBound" : BoundingType.UP_TO_NEXT, "endBoundEntity" : qUnion([Q1]), "depth" : 25 * mm, "hasSecondDirection" : true, "secondDirectionBound" : SecondDirectionBoundingType.UP_TO_NEXT, "secondDirectionOppositeDirection" : true, "secondDirectionBoundEntity" : qUnion([Q2]), "secondDirectionDepth" : 25 * mm});
        }
        {
            var Q0;
            Q0=makeQuery(id+"F23.opExtrude","SWEPT_FACE",FACE,{"disambiguationData":[OSD([sQuery(id+"F22.wireOp",EDGE,"E83.top")])]});
            cPlane(context, id + "F32", {"entities" : qUnion([Q0]), "cplaneType" : CPlaneType.OFFSET, "offset" : 500 * mm, "width" : 150 * mm, "height" : 150 * mm});
        }
        {
            var Q0;
            Q0=qCreatedBy(id+"F32.planeOp",FACE);
            var sketch = newSketch(context, id + "F33", { "sketchPlane" : qUnion([Q0])});
            skPoint(sketch, "E118.0", {"position": v(-50, -1040) * mm});
            skPoint(sketch, "E119.0", {"position": v(1430, -990) * mm});
            skLineSegment(sketch, "E120.bottom", {"start": v(-50, -1040) * mm, "end": v(1430, -1040) * mm, "construction": true});
            skLineSegment(sketch, "E120.top", {"start": v(-50, -990) * mm, "end": v(1430, -990) * mm, "construction": true});
            skLineSegment(sketch, "E120.left", {"start": v(-50, -1040) * mm, "end": v(-50, -990) * mm, "construction": true});
            skLineSegment(sketch, "E120.right", {"start": v(1430, -1040) * mm, "end": v(1430, -990) * mm, "construction": true});
            skPoint(sketch, "E121", {"position": v(690, -1040) * mm});
            skLineSegment(sketch, "E122.bottom", {"start": v(665, -1040) * mm, "end": v(715, -1040) * mm});
            skLineSegment(sketch, "E122.top", {"start": v(665, -990) * mm, "end": v(715, -990) * mm});
            skLineSegment(sketch, "E122.left", {"start": v(665, -1040) * mm, "end": v(665, -990) * mm});
            skLineSegment(sketch, "E122.right", {"start": v(715, -1040) * mm, "end": v(715, -990) * mm});
            skSolve(sketch);
        }
        {
            var Q0;
            Q0=makeQuery(id+"F33.imprint","IMPRINT",FACE,{"disambiguationData":[TD([[makeQuery(id+"F33.imprint","IMPRINT",EDGE,{"derivedFrom":sQuery(id+"F33.wireOp",EDGE,"E122.bottom")}),1.0]])]});
            var Q1;
            Q1=makeQuery(id+"F26.boolean.opBoolean","MERGE",FACE,{"derivedFrom":[makeQuery(id+"F5.opExtrude","SWEPT_FACE",FACE,{"disambiguationData":[OSD([sQuery(id+"F4.wireOp",EDGE,"E12.top")])]}),makeQuery(id+"F26.opExtrude","SWEPT_FACE",FACE,{"disambiguationData":[OSD([sQuery(id+"F25.wireOp",EDGE,"E91.top")])]}),makeQuery(id+"F26.opExtrude","SWEPT_FACE",FACE,{"disambiguationData":[OSD([sQuery(id+"F25.wireOp",EDGE,"E93.top")])]})]});
            var Q2;
            Q2=makeQuery(id+"F29.opExtrude","SWEPT_FACE",FACE,{"disambiguationData":[OSD([sQuery(id+"F28.wireOp",EDGE,"E106.bottom")])]});
            extrude(context, id + "F34", {"entities" : qUnion([Q0]), "operationType" : NewBodyOperationType.ADD, "endBound" : BoundingType.UP_TO_NEXT, "endBoundEntity" : qUnion([Q1]), "depth" : 25 * mm, "hasSecondDirection" : true, "secondDirectionBound" : SecondDirectionBoundingType.UP_TO_NEXT, "secondDirectionOppositeDirection" : true, "secondDirectionBoundEntity" : qUnion([Q2]), "secondDirectionDepth" : 25 * mm});
        }
        {
            var Q0;
            Q0=qCreatedBy(id+"F32.planeOp",FACE);
            var sketch = newSketch(context, id + "F35", { "sketchPlane" : qUnion([Q0])});
            skPoint(sketch, "E123.0", {"position": v(-50, 20) * mm});
            skPoint(sketch, "E124.0", {"position": v(1430, -20) * mm});
            skLineSegment(sketch, "E125.bottom", {"start": v(1430, -20) * mm, "end": v(-50, -20) * mm, "construction": true});
            skLineSegment(sketch, "E125.top", {"start": v(1430, 20) * mm, "end": v(-50, 20) * mm, "construction": true});
            skLineSegment(sketch, "E125.left", {"start": v(1430, -20) * mm, "end": v(1430, 20) * mm, "construction": true});
            skLineSegment(sketch, "E125.right", {"start": v(-50, -20) * mm, "end": v(-50, 20) * mm, "construction": true});
            skPoint(sketch, "E126", {"position": v(690, 20) * mm});
            skLineSegment(sketch, "E127.bottom", {"start": v(710, -25) * mm, "end": v(670, -25) * mm});
            skLineSegment(sketch, "E127.top", {"start": v(710, 25) * mm, "end": v(670, 25) * mm});
            skLineSegment(sketch, "E127.left", {"start": v(715, -20) * mm, "end": v(715, 20) * mm});
            skLineSegment(sketch, "E127.right", {"start": v(665, -20) * mm, "end": v(665, 20) * mm});
            skPoint(sketch, "E128.visualSharp", {"position": v(715, 25) * mm});
            skArc(sketch, "E128.filletArc", {"start": v(715, 20) * mm, "mid": v(713.54, 23.54) * mm, "end": v(710, 25) * mm});
            skPoint(sketch, "E129.visualSharp", {"position": v(715, -25) * mm});
            skArc(sketch, "E129.filletArc", {"start": v(710, -25) * mm, "mid": v(713.54, -23.54) * mm, "end": v(715, -20) * mm});
            skPoint(sketch, "E130.visualSharp", {"position": v(665, -25) * mm});
            skArc(sketch, "E130.filletArc", {"start": v(665, -20) * mm, "mid": v(666.46, -23.54) * mm, "end": v(670, -25) * mm});
            skPoint(sketch, "E131.visualSharp", {"position": v(665, 25) * mm});
            skArc(sketch, "E131.filletArc", {"start": v(670, 25) * mm, "mid": v(666.46, 23.54) * mm, "end": v(665, 20) * mm});
            skLineSegment(sketch, "E132", {"start": v(715, 20) * mm, "end": v(665, 20) * mm, "construction": true});
            skSolve(sketch);
        }
        {
            var Q0;
            Q0=makeQuery(id+"F35.imprint","IMPRINT",FACE,{"disambiguationData":[TD([[makeQuery(id+"F35.imprint","IMPRINT",EDGE,{"derivedFrom":sQuery(id+"F35.wireOp",EDGE,"E127.bottom")}),-1.0]])]});
            var Q1;
            Q1=makeQuery(id+"F5.opExtrude","SWEPT_FACE",FACE,{"disambiguationData":[OSD([sQuery(id+"F4.wireOp",EDGE,"E20.top")])]});
            var Q2;
            Q2=makeQuery(id+"F31.opExtrude","SWEPT_FACE",FACE,{"disambiguationData":[OSD([sQuery(id+"F30.wireOp",EDGE,"E113.bottom")])]});
            extrude(context, id + "F36", {"entities" : qUnion([Q0]), "operationType" : NewBodyOperationType.ADD, "endBound" : BoundingType.UP_TO_SURFACE, "endBoundEntityFace" : qUnion([Q1]), "depth" : 25 * mm, "hasSecondDirection" : true, "secondDirectionBound" : SecondDirectionBoundingType.UP_TO_SURFACE, "secondDirectionOppositeDirection" : true, "secondDirectionBoundEntityFace" : qUnion([Q2]), "secondDirectionDepth" : 25 * mm});
        }
        {
            var Q0;
            {var subQ5=sQuery(id+"F4.wireOp",EDGE,"E12.right");Q0=makeQuery(id+"F19.boolean.opBoolean","SPLIT",FACE,{"disambiguationData":[TD([makeQuery(id+"F5.opExtrude","SWEPT_FACE",FACE,{"disambiguationData":[OSD([subQ5])]})])],"derivedFrom":makeQuery(id+"F19.opExtrude","SWEPT_FACE",FACE,{"disambiguationData":[OSD([sQuery(id+"F18.wireOp",EDGE,"E67.left")])]})});}
            cPlane(context, id + "F37", {"entities" : qUnion([Q0]), "cplaneType" : CPlaneType.OFFSET, "offset" : 150 * mm, "width" : 150 * mm, "height" : 150 * mm});
        }
        {
            var Q0;
            Q0=qCreatedBy(id+"F37.planeOp",FACE);
            var sketch = newSketch(context, id + "F38", { "sketchPlane" : qUnion([Q0])});
            skPoint(sketch, "E133.0", {"position": v(-945, -150) * mm});
            skPoint(sketch, "E134.0", {"position": v(-70, -200) * mm});
            skLineSegment(sketch, "E135.bottom", {"start": v(-945, -150) * mm, "end": v(-70, -150) * mm, "construction": true});
            skLineSegment(sketch, "E135.top", {"start": v(-945, -200) * mm, "end": v(-70, -200) * mm, "construction": true});
            skLineSegment(sketch, "E135.left", {"start": v(-945, -150) * mm, "end": v(-945, -200) * mm, "construction": true});
            skLineSegment(sketch, "E135.right", {"start": v(-70, -150) * mm, "end": v(-70, -200) * mm, "construction": true});
            skPoint(sketch, "E136", {"position": v(-507.5, -200) * mm});
            skLineSegment(sketch, "E137.bottom", {"start": v(-527.5, -150) * mm, "end": v(-487.5, -150) * mm});
            skLineSegment(sketch, "E137.top", {"start": v(-527.5, -200) * mm, "end": v(-487.5, -200) * mm});
            skLineSegment(sketch, "E137.left", {"start": v(-532.5, -155) * mm, "end": v(-532.5, -195) * mm});
            skLineSegment(sketch, "E137.right", {"start": v(-482.5, -155) * mm, "end": v(-482.5, -195) * mm});
            skPoint(sketch, "E138.visualSharp", {"position": v(-532.5, -150) * mm});
            skArc(sketch, "E138.filletArc", {"start": v(-527.5, -150) * mm, "mid": v(-531.04, -151.46) * mm, "end": v(-532.5, -155) * mm});
            skPoint(sketch, "E139.visualSharp", {"position": v(-482.5, -150) * mm});
            skArc(sketch, "E139.filletArc", {"start": v(-482.5, -155) * mm, "mid": v(-483.96, -151.46) * mm, "end": v(-487.5, -150) * mm});
            skPoint(sketch, "E140.visualSharp", {"position": v(-482.5, -200) * mm});
            skArc(sketch, "E140.filletArc", {"start": v(-487.5, -200) * mm, "mid": v(-483.96, -198.54) * mm, "end": v(-482.5, -195) * mm});
            skPoint(sketch, "E141.visualSharp", {"position": v(-532.5, -200) * mm});
            skArc(sketch, "E141.filletArc", {"start": v(-532.5, -195) * mm, "mid": v(-531.04, -198.54) * mm, "end": v(-527.5, -200) * mm});
            skSolve(sketch);
        }
        {
            var Q0;
            Q0=makeQuery(id+"F38.imprint","IMPRINT",FACE,{"disambiguationData":[TD([[makeQuery(id+"F38.imprint","IMPRINT",EDGE,{"derivedFrom":sQuery(id+"F38.wireOp",EDGE,"E137.bottom")}),-1.0]])]});
            var Q1;
            {var subQ3=sQuery(id+"F4.wireOp",EDGE,"E12.right");Q1=makeQuery(id+"F17.boolean.opBoolean","SPLIT",FACE,{"disambiguationData":[TD([makeQuery(id+"F5.opExtrude","SWEPT_FACE",FACE,{"disambiguationData":[OSD([subQ3])]})])],"derivedFrom":makeQuery(id+"F17.opExtrude","SWEPT_FACE",FACE,{"disambiguationData":[OSD([sQuery(id+"F16.wireOp",EDGE,"E59.left")])]})});}
            extrude(context, id + "F39", {"entities" : qUnion([Q0]), "operationType" : NewBodyOperationType.ADD, "endBound" : BoundingType.UP_TO_SURFACE, "endBoundEntityFace" : qUnion([Q1]), "depth" : 25 * mm, "hasSecondDirection" : true, "secondDirectionBound" : SecondDirectionBoundingType.UP_TO_NEXT, "secondDirectionOppositeDirection" : true, "secondDirectionDepth" : 25 * mm});
        }
        {
            var Q0;
            Q0=makeQuery(id+"F21.boolean.opBoolean","MERGE",FACE,{"derivedFrom":[makeQuery(id+"F17.boolean.opBoolean","MERGE",FACE,{"derivedFrom":[makeQuery(id+"F8.boolean.opBoolean","MERGE",FACE,{"derivedFrom":[makeQuery(id+"F2.opExtrude","CAP_FACE",FACE,{"disambiguationData":[OSD([sQuery(id+"F1.wireOp",EDGE,"E6.rect.bottom"),sQuery(id+"F1.wireOp",EDGE,"E6.rect.top"),sQuery(id+"F1.wireOp",EDGE,"E6.rect.left"),sQuery(id+"F1.wireOp",EDGE,"E6.rect.right"),sQuery(id+"F1.wireOp",EDGE,"E7.filletArc"),sQuery(id+"F1.wireOp",EDGE,"E8.filletArc"),sQuery(id+"F1.wireOp",EDGE,"E9.filletArc"),sQuery(id+"F1.wireOp",EDGE,"E10.filletArc"),sQuery(id+"F1.wireOp",EDGE,"E11.0"),sQuery(id+"F1.wireOp",EDGE,"E11.1"),sQuery(id+"F1.wireOp",EDGE,"E11.2"),sQuery(id+"F1.wireOp",EDGE,"E11.3")])],"isStart":false}),makeQuery(id+"F8.opExtrude","SWEPT_FACE",FACE,{"disambiguationData":[OSD([sQuery(id+"F7.wireOp",EDGE,"E29.right")])]})]}),makeQuery(id+"F17.opExtrude","SWEPT_FACE",FACE,{"disambiguationData":[OSD([sQuery(id+"F16.wireOp",EDGE,"E59.right")])]})]}),makeQuery(id+"F21.opExtrude","SWEPT_FACE",FACE,{"disambiguationData":[OSD([sQuery(id+"F20.wireOp",EDGE,"E75.right")])]})]});
            cPlane(context, id + "F40", {"entities" : qUnion([Q0]), "cplaneType" : CPlaneType.OFFSET, "offset" : 0 * mm, "width" : 150 * mm, "height" : 150 * mm});
        }
        {
            var Q0;
            Q0=qCreatedBy(id+"F40.planeOp",FACE);
            var sketch = newSketch(context, id + "F41", { "sketchPlane" : qUnion([Q0])});
            skLineSegment(sketch, "E142.0", {"start": v(-995, 50) * mm, "end": v(-1035, 50) * mm, "construction": true});
            skPoint(sketch, "E143", {"position": v(-1015, 50) * mm});
            skLineSegment(sketch, "E144.0", {"start": v(20, 50) * mm, "end": v(-20, 50) * mm, "construction": true});
            skPoint(sketch, "E145", {"position": v(0, 50) * mm});
            skLineSegment(sketch, "E146.bottom", {"start": v(-10, 50) * mm, "end": v(10, 50) * mm, "construction": true});
            skLineSegment(sketch, "E146.top", {"start": v(-10, 68) * mm, "end": v(10, 68) * mm, "construction": true});
            skLineSegment(sketch, "E146.left", {"start": v(-10, 50) * mm, "end": v(-10, 68) * mm, "construction": true});
            skLineSegment(sketch, "E146.right", {"start": v(10, 50) * mm, "end": v(10, 68) * mm, "construction": true});
            skLineSegment(sketch, "E147", {"start": v(-10, 64.5) * mm, "end": v(10, 64.5) * mm, "construction": true});
            skPoint(sketch, "E148", {"position": v(0, 64.5) * mm});
            skLineSegment(sketch, "E149.rect.bottom", {"start": v(20, 67.5) * mm, "end": v(-10, 67.5) * mm, "construction": true});
            skLineSegment(sketch, "E149.rect.top", {"start": v(10, 61.5) * mm, "end": v(-20, 61.5) * mm, "construction": true});
            skArc(sketch, "E150", {"start": v(-10, 65.4) * mm, "mid": v(-8.52, 66.02) * mm, "end": v(-7.9, 67.5) * mm});
            skArc(sketch, "E151.0.MirrorCS", {"start": v(-10, 63.6) * mm, "mid": v(-8.52, 62.98) * mm, "end": v(-7.9, 61.5) * mm});
            skLineSegment(sketch, "E152", {"start": v(0, 64.5) * mm, "end": v(0, 50) * mm, "construction": true});
            skArc(sketch, "E153.0.MirrorCS", {"start": v(10, 63.6) * mm, "mid": v(8.52, 62.98) * mm, "end": v(7.9, 61.5) * mm});
            skArc(sketch, "E153.1.MirrorCS", {"start": v(10, 65.4) * mm, "mid": v(8.52, 66.02) * mm, "end": v(7.9, 67.5) * mm});
            skLineSegment(sketch, "E154", {"start": v(-7.9, 67.5) * mm, "end": v(-7.4, 68) * mm});
            skLineSegment(sketch, "E155", {"start": v(-7.4, 68) * mm, "end": v(7.4, 68) * mm});
            skLineSegment(sketch, "E156", {"start": v(7.4, 68) * mm, "end": v(7.9, 67.5) * mm});
            skPoint(sketch, "E157", {"position": v(0, 68) * mm});
            skLineSegment(sketch, "E158.bottom", {"start": v(-6.55, 60.5) * mm, "end": v(6.55, 60.5) * mm, "construction": true});
            skLineSegment(sketch, "E158.top", {"start": v(-6.55, 57.5) * mm, "end": v(6.55, 57.5) * mm, "construction": true});
            skLineSegment(sketch, "E158.left", {"start": v(-6.55, 60.5) * mm, "end": v(-6.55, 57.5) * mm, "construction": true});
            skLineSegment(sketch, "E158.right", {"start": v(6.55, 60.5) * mm, "end": v(6.55, 57.5) * mm, "construction": true});
            skPoint(sketch, "E159", {"position": v(0, 57.5) * mm});
            skLineSegment(sketch, "E160", {"start": v(-7.9, 61.5) * mm, "end": v(-6.55, 60.5) * mm});
            skLineSegment(sketch, "E161", {"start": v(6.55, 60.5) * mm, "end": v(7.9, 61.5) * mm});
            skLineSegment(sketch, "E162", {"start": v(6.55, 60.5) * mm, "end": v(6.55, 57.5) * mm});
            skLineSegment(sketch, "E163", {"start": v(-6.55, 57.5) * mm, "end": v(-6.55, 60.5) * mm});
            skLineSegment(sketch, "E164", {"start": v(-10, 54) * mm, "end": v(-10, 50.5) * mm});
            skLineSegment(sketch, "E165", {"start": v(-9.5, 50) * mm, "end": v(-2, 50) * mm});
            skLineSegment(sketch, "E166", {"start": v(10, 50.5) * mm, "end": v(10, 54) * mm});
            skLineSegment(sketch, "E167", {"start": v(-6.55, 57.5) * mm, "end": v(-10, 54) * mm});
            skLineSegment(sketch, "E168", {"start": v(10, 54) * mm, "end": v(6.55, 57.5) * mm});
            skCircle(sketch, "E169", {"center": v(-10, 50) * mm, "radius": 0.5 * mm, "construction": true});
            skCircle(sketch, "E170", {"center": v(10, 50) * mm, "radius": 0.5 * mm, "construction": true});
            skLineSegment(sketch, "E171", {"start": v(-10, 50.5) * mm, "end": v(-9.5, 50) * mm});
            skLineSegment(sketch, "E172", {"start": v(10, 50.5) * mm, "end": v(9.5, 50) * mm});
            skLineSegment(sketch, "E173.trimOffspring", {"start": v(2, 50) * mm, "end": v(9.5, 50) * mm});
            skLineSegment(sketch, "E174", {"start": v(-1.5, 50.5) * mm, "end": v(1.5, 50.5) * mm});
            skPoint(sketch, "E175", {"position": v(0, 50.5) * mm});
            skLineSegment(sketch, "E176", {"start": v(2, 50) * mm, "end": v(1.5, 50.5) * mm});
            skLineSegment(sketch, "E177", {"start": v(-1.5, 50.5) * mm, "end": v(-2, 50) * mm});
            skLineSegment(sketch, "E178", {"start": v(-10, 63.6) * mm, "end": v(-10, 65.4) * mm});
            skLineSegment(sketch, "E179", {"start": v(10, 65.4) * mm, "end": v(10, 63.6) * mm});
            skLineSegment(sketch, "E180.bottom", {"start": v(-1025, 50) * mm, "end": v(-1005, 50) * mm, "construction": true});
            skLineSegment(sketch, "E180.top", {"start": v(-1025, 68) * mm, "end": v(-1005, 68) * mm, "construction": true});
            skLineSegment(sketch, "E180.left", {"start": v(-1025, 50) * mm, "end": v(-1025, 68) * mm, "construction": true});
            skLineSegment(sketch, "E180.right", {"start": v(-1005, 50) * mm, "end": v(-1005, 68) * mm, "construction": true});
            skLineSegment(sketch, "E181", {"start": v(-1025, 64.5) * mm, "end": v(-1005, 64.5) * mm, "construction": true});
            skPoint(sketch, "E182", {"position": v(-1015, 64.5) * mm});
            skLineSegment(sketch, "E183.rect.bottom", {"start": v(20, 67.5) * mm, "end": v(-1025, 67.5) * mm, "construction": true});
            skLineSegment(sketch, "E183.rect.top", {"start": v(-1005, 61.5) * mm, "end": v(-2050, 61.5) * mm, "construction": true});
            skArc(sketch, "E184", {"start": v(-1025, 65.4) * mm, "mid": v(-1023.52, 66.02) * mm, "end": v(-1022.9, 67.5) * mm});
            skArc(sketch, "E185.0.MirrorCS", {"start": v(-1025, 63.6) * mm, "mid": v(-1023.52, 62.98) * mm, "end": v(-1022.9, 61.5) * mm});
            skLineSegment(sketch, "E186", {"start": v(-1015, 64.5) * mm, "end": v(-1015, 50) * mm, "construction": true});
            skArc(sketch, "E187.0.MirrorCS", {"start": v(-1005, 63.6) * mm, "mid": v(-1006.48, 62.98) * mm, "end": v(-1007.1, 61.5) * mm});
            skArc(sketch, "E187.1.MirrorCS", {"start": v(-1005, 65.4) * mm, "mid": v(-1006.48, 66.02) * mm, "end": v(-1007.1, 67.5) * mm});
            skLineSegment(sketch, "E188", {"start": v(-1022.9, 67.5) * mm, "end": v(-1022.4, 68) * mm});
            skLineSegment(sketch, "E189", {"start": v(-1022.4, 68) * mm, "end": v(-1007.6, 68) * mm});
            skLineSegment(sketch, "E190", {"start": v(-1007.6, 68) * mm, "end": v(-1007.1, 67.5) * mm});
            skPoint(sketch, "E191", {"position": v(-1015, 68) * mm});
            skLineSegment(sketch, "E192.bottom", {"start": v(-1021.55, 60.5) * mm, "end": v(-1008.45, 60.5) * mm, "construction": true});
            skLineSegment(sketch, "E192.top", {"start": v(-1021.55, 57.5) * mm, "end": v(-1008.45, 57.5) * mm, "construction": true});
            skLineSegment(sketch, "E192.left", {"start": v(-1021.55, 60.5) * mm, "end": v(-1021.55, 57.5) * mm, "construction": true});
            skLineSegment(sketch, "E192.right", {"start": v(-1008.45, 60.5) * mm, "end": v(-1008.45, 57.5) * mm, "construction": true});
            skPoint(sketch, "E193", {"position": v(-1015, 57.5) * mm});
            skLineSegment(sketch, "E194", {"start": v(-1022.9, 61.5) * mm, "end": v(-1021.55, 60.5) * mm});
            skLineSegment(sketch, "E195", {"start": v(-1008.45, 60.5) * mm, "end": v(-1007.1, 61.5) * mm});
            skLineSegment(sketch, "E196", {"start": v(-1008.45, 60.5) * mm, "end": v(-1008.45, 57.5) * mm});
            skLineSegment(sketch, "E197", {"start": v(-1021.55, 57.5) * mm, "end": v(-1021.55, 60.5) * mm});
            skLineSegment(sketch, "E198", {"start": v(-1025, 54) * mm, "end": v(-1025, 50.5) * mm});
            skLineSegment(sketch, "E199", {"start": v(-1024.5, 50) * mm, "end": v(-1017, 50) * mm});
            skLineSegment(sketch, "E200", {"start": v(-1005, 50.5) * mm, "end": v(-1005, 54) * mm});
            skLineSegment(sketch, "E201", {"start": v(-1021.55, 57.5) * mm, "end": v(-1025, 54) * mm});
            skLineSegment(sketch, "E202", {"start": v(-1005, 54) * mm, "end": v(-1008.45, 57.5) * mm});
            skCircle(sketch, "E203", {"center": v(-1025, 50) * mm, "radius": 0.5 * mm, "construction": true});
            skCircle(sketch, "E204", {"center": v(-1005, 50) * mm, "radius": 0.5 * mm, "construction": true});
            skLineSegment(sketch, "E205", {"start": v(-1025, 50.5) * mm, "end": v(-1024.5, 50) * mm});
            skLineSegment(sketch, "E206", {"start": v(-1005, 50.5) * mm, "end": v(-1005.5, 50) * mm});
            skLineSegment(sketch, "E207.trimOffspring", {"start": v(-1013, 50) * mm, "end": v(-1005.5, 50) * mm});
            skLineSegment(sketch, "E208", {"start": v(-1016.5, 50.5) * mm, "end": v(-1013.5, 50.5) * mm});
            skPoint(sketch, "E209", {"position": v(-1015, 50.5) * mm});
            skLineSegment(sketch, "E210", {"start": v(-1013, 50) * mm, "end": v(-1013.5, 50.5) * mm});
            skLineSegment(sketch, "E211", {"start": v(-1016.5, 50.5) * mm, "end": v(-1017, 50) * mm});
            skLineSegment(sketch, "E212", {"start": v(-1025, 63.6) * mm, "end": v(-1025, 65.4) * mm});
            skLineSegment(sketch, "E213", {"start": v(-1005, 65.4) * mm, "end": v(-1005, 63.6) * mm});
            skSolve(sketch);
        }
        {
            var Q0;
            Q0=makeQuery(id+"F41.imprint","IMPRINT",FACE,{"disambiguationData":[TD([[makeQuery(id+"F41.imprint","IMPRINT",EDGE,{"derivedFrom":sQuery(id+"F41.wireOp",EDGE,"E184")}),-1.0]])]});
            var Q1;
            Q1=makeQuery(id+"F41.imprint","IMPRINT",FACE,{"disambiguationData":[TD([[makeQuery(id+"F41.imprint","IMPRINT",EDGE,{"derivedFrom":sQuery(id+"F41.wireOp",EDGE,"E150")}),-1.0]])]});
            var Q2;
            Q2=makeQuery(id+"F2.opExtrude","CAP_FACE",FACE,{"disambiguationData":[OSD([sQuery(id+"F1.wireOp",EDGE,"E6.rect.bottom"),sQuery(id+"F1.wireOp",EDGE,"E6.rect.top"),sQuery(id+"F1.wireOp",EDGE,"E6.rect.left"),sQuery(id+"F1.wireOp",EDGE,"E6.rect.right"),sQuery(id+"F1.wireOp",EDGE,"E7.filletArc"),sQuery(id+"F1.wireOp",EDGE,"E8.filletArc"),sQuery(id+"F1.wireOp",EDGE,"E9.filletArc"),sQuery(id+"F1.wireOp",EDGE,"E10.filletArc"),sQuery(id+"F1.wireOp",EDGE,"E11.0"),sQuery(id+"F1.wireOp",EDGE,"E11.1"),sQuery(id+"F1.wireOp",EDGE,"E11.2"),sQuery(id+"F1.wireOp",EDGE,"E11.3")])],"isStart":true});
            extrude(context, id + "F42", {"entities" : qUnion([Q0, Q1]), "endBound" : BoundingType.UP_TO_SURFACE, "oppositeDirection" : true, "endBoundEntityFace" : qUnion([Q2]), "depth" : 25 * mm});
        }
        {
            var Q0;
            Q0=makeQuery(id+"F39.boolean.opBoolean","MERGE",FACE,{"derivedFrom":[makeQuery(id+"F19.opExtrude","SWEPT_FACE",FACE,{"disambiguationData":[OSD([sQuery(id+"F18.wireOp",EDGE,"E67.bottom")])]}),makeQuery(id+"F26.boolean.opBoolean","MERGE",FACE,{"derivedFrom":[makeQuery(id+"F5.opExtrude","SWEPT_FACE",FACE,{"disambiguationData":[OSD([sQuery(id+"F4.wireOp",EDGE,"E12.bottom")])]}),makeQuery(id+"F26.opExtrude","SWEPT_FACE",FACE,{"disambiguationData":[OSD([sQuery(id+"F25.wireOp",EDGE,"E91.bottom")])]}),makeQuery(id+"F26.opExtrude","SWEPT_FACE",FACE,{"disambiguationData":[OSD([sQuery(id+"F25.wireOp",EDGE,"E93.bottom")])]})]}),makeQuery(id+"F39.opExtrude","SWEPT_FACE",FACE,{"disambiguationData":[OSD([sQuery(id+"F38.wireOp",EDGE,"E137.bottom")])]})]});
            cPlane(context, id + "F43", {"entities" : qUnion([Q0]), "cplaneType" : CPlaneType.OFFSET, "offset" : 0 * mm, "width" : 150 * mm, "height" : 150 * mm});
        }
        {
            var Q0;
            Q0=qCreatedBy(id+"F43.planeOp",FACE);
            var sketch = newSketch(context, id + "F44", { "sketchPlane" : qUnion([Q0])});
            skPoint(sketch, "E214.0", {"position": v(-50, -1040) * mm});
            skPoint(sketch, "E215.0", {"position": v(1435, -990) * mm});
            skLineSegment(sketch, "E216.bottom", {"start": v(1435, -990) * mm, "end": v(-50, -990) * mm, "construction": true});
            skLineSegment(sketch, "E216.top", {"start": v(1435, -1040) * mm, "end": v(-50, -1040) * mm, "construction": true});
            skLineSegment(sketch, "E216.left", {"start": v(1435, -990) * mm, "end": v(1435, -1040) * mm, "construction": true});
            skLineSegment(sketch, "E216.right", {"start": v(-50, -990) * mm, "end": v(-50, -1040) * mm, "construction": true});
            skLineSegment(sketch, "E217.0", {"start": v(410, -1040) * mm, "end": v(410, -532.5) * mm, "construction": true});
            skLineSegment(sketch, "E218.0", {"start": v(460, -1040) * mm, "end": v(460, -532.5) * mm, "construction": true});
            skPoint(sketch, "E219.orphan", {"position": v(410, -940) * mm});
            skPoint(sketch, "E220.orphan", {"position": v(460, -940) * mm});
            skLineSegment(sketch, "E221.bottom", {"start": v(415, -990) * mm, "end": v(455, -990) * mm});
            skLineSegment(sketch, "E221.top", {"start": v(415, -1040) * mm, "end": v(455, -1040) * mm});
            skLineSegment(sketch, "E221.left", {"start": v(410, -995) * mm, "end": v(410, -1035) * mm});
            skLineSegment(sketch, "E221.right", {"start": v(460, -995) * mm, "end": v(460, -1035) * mm});
            skLineSegment(sketch, "E222.0", {"start": v(920, -1040) * mm, "end": v(920, -532.5) * mm, "construction": true});
            skLineSegment(sketch, "E223.0", {"start": v(970, -1040) * mm, "end": v(970, -532.5) * mm, "construction": true});
            skPoint(sketch, "E224.orphan", {"position": v(920, -940) * mm});
            skPoint(sketch, "E225.orphan", {"position": v(970, -940) * mm});
            skLineSegment(sketch, "E226.bottom", {"start": v(925, -990) * mm, "end": v(965, -990) * mm});
            skLineSegment(sketch, "E226.top", {"start": v(925, -1040) * mm, "end": v(965, -1040) * mm});
            skLineSegment(sketch, "E226.left", {"start": v(920, -995) * mm, "end": v(920, -1035) * mm});
            skLineSegment(sketch, "E226.right", {"start": v(970, -995) * mm, "end": v(970, -1035) * mm});
            skPoint(sketch, "E227.0", {"position": v(-55, -25) * mm});
            skPoint(sketch, "E228.0", {"position": v(1430, 25) * mm});
            skLineSegment(sketch, "E229.bottom", {"start": v(1430, 25) * mm, "end": v(-55, 25) * mm, "construction": true});
            skLineSegment(sketch, "E229.top", {"start": v(1430, -25) * mm, "end": v(-55, -25) * mm, "construction": true});
            skLineSegment(sketch, "E229.left", {"start": v(1430, 25) * mm, "end": v(1430, -25) * mm, "construction": true});
            skLineSegment(sketch, "E229.right", {"start": v(-55, 25) * mm, "end": v(-55, -25) * mm, "construction": true});
            skLineSegment(sketch, "E230.0", {"start": v(410, -482.5) * mm, "end": v(410, 25) * mm, "construction": true});
            skLineSegment(sketch, "E231.0", {"start": v(460, -482.5) * mm, "end": v(460, 25) * mm, "construction": true});
            skPoint(sketch, "E232.orphan", {"position": v(460, -75) * mm});
            skPoint(sketch, "E233.orphan", {"position": v(410, -75) * mm});
            skLineSegment(sketch, "E234.bottom", {"start": v(415, 25) * mm, "end": v(455, 25) * mm});
            skLineSegment(sketch, "E234.top", {"start": v(415, -25) * mm, "end": v(455, -25) * mm});
            skLineSegment(sketch, "E234.left", {"start": v(410, 20) * mm, "end": v(410, -20) * mm});
            skLineSegment(sketch, "E234.right", {"start": v(460, 20) * mm, "end": v(460, -20) * mm});
            skLineSegment(sketch, "E235.0", {"start": v(970, -482.5) * mm, "end": v(970, 25) * mm, "construction": true});
            skLineSegment(sketch, "E236.0", {"start": v(920, -482.5) * mm, "end": v(920, 25) * mm, "construction": true});
            skPoint(sketch, "E237.orphan", {"position": v(920, -75) * mm});
            skPoint(sketch, "E238.orphan", {"position": v(970, -75) * mm});
            skLineSegment(sketch, "E239.bottom", {"start": v(925, 25) * mm, "end": v(965, 25) * mm});
            skLineSegment(sketch, "E239.top", {"start": v(925, -25) * mm, "end": v(965, -25) * mm});
            skLineSegment(sketch, "E239.left", {"start": v(920, 20) * mm, "end": v(920, -20) * mm});
            skLineSegment(sketch, "E239.right", {"start": v(970, 20) * mm, "end": v(970, -20) * mm});
            skPoint(sketch, "E240.visualSharp", {"position": v(410, -990) * mm});
            skArc(sketch, "E240.filletArc", {"start": v(415, -990) * mm, "mid": v(411.46, -991.46) * mm, "end": v(410, -995) * mm});
            skPoint(sketch, "E241.visualSharp", {"position": v(460, -990) * mm});
            skArc(sketch, "E241.filletArc", {"start": v(460, -995) * mm, "mid": v(458.54, -991.46) * mm, "end": v(455, -990) * mm});
            skPoint(sketch, "E242.visualSharp", {"position": v(410, -1040) * mm});
            skArc(sketch, "E242.filletArc", {"start": v(410, -1035) * mm, "mid": v(411.46, -1038.54) * mm, "end": v(415, -1040) * mm});
            skPoint(sketch, "E243.visualSharp", {"position": v(460, -1040) * mm});
            skArc(sketch, "E243.filletArc", {"start": v(455, -1040) * mm, "mid": v(458.54, -1038.54) * mm, "end": v(460, -1035) * mm});
            skPoint(sketch, "E244.visualSharp", {"position": v(920, -990) * mm});
            skArc(sketch, "E244.filletArc", {"start": v(925, -990) * mm, "mid": v(921.46, -991.46) * mm, "end": v(920, -995) * mm});
            skPoint(sketch, "E245.visualSharp", {"position": v(970, -990) * mm});
            skArc(sketch, "E245.filletArc", {"start": v(970, -995) * mm, "mid": v(968.54, -991.46) * mm, "end": v(965, -990) * mm});
            skPoint(sketch, "E246.visualSharp", {"position": v(970, -1040) * mm});
            skArc(sketch, "E246.filletArc", {"start": v(965, -1040) * mm, "mid": v(968.54, -1038.54) * mm, "end": v(970, -1035) * mm});
            skPoint(sketch, "E247.visualSharp", {"position": v(920, -1040) * mm});
            skArc(sketch, "E247.filletArc", {"start": v(920, -1035) * mm, "mid": v(921.46, -1038.54) * mm, "end": v(925, -1040) * mm});
            skPoint(sketch, "E248.visualSharp", {"position": v(410, 25) * mm});
            skArc(sketch, "E248.filletArc", {"start": v(415, 25) * mm, "mid": v(411.46, 23.54) * mm, "end": v(410, 20) * mm});
            skPoint(sketch, "E249.visualSharp", {"position": v(460, 25) * mm});
            skArc(sketch, "E249.filletArc", {"start": v(460, 20) * mm, "mid": v(458.54, 23.54) * mm, "end": v(455, 25) * mm});
            skPoint(sketch, "E250.visualSharp", {"position": v(460, -25) * mm});
            skArc(sketch, "E250.filletArc", {"start": v(455, -25) * mm, "mid": v(458.54, -23.54) * mm, "end": v(460, -20) * mm});
            skPoint(sketch, "E251.visualSharp", {"position": v(410, -25) * mm});
            skArc(sketch, "E251.filletArc", {"start": v(410, -20) * mm, "mid": v(411.46, -23.54) * mm, "end": v(415, -25) * mm});
            skPoint(sketch, "E252.visualSharp", {"position": v(920, 25) * mm});
            skArc(sketch, "E252.filletArc", {"start": v(925, 25) * mm, "mid": v(921.46, 23.54) * mm, "end": v(920, 20) * mm});
            skPoint(sketch, "E253.visualSharp", {"position": v(970, 25) * mm});
            skArc(sketch, "E253.filletArc", {"start": v(970, 20) * mm, "mid": v(968.54, 23.54) * mm, "end": v(965, 25) * mm});
            skPoint(sketch, "E254.visualSharp", {"position": v(970, -25) * mm});
            skArc(sketch, "E254.filletArc", {"start": v(965, -25) * mm, "mid": v(968.54, -23.54) * mm, "end": v(970, -20) * mm});
            skPoint(sketch, "E255.visualSharp", {"position": v(920, -25) * mm});
            skArc(sketch, "E255.filletArc", {"start": v(920, -20) * mm, "mid": v(921.46, -23.54) * mm, "end": v(925, -25) * mm});
            skSolve(sketch);
        }
        {
            var Q0;
            Q0=makeQuery(id+"F44.imprint","IMPRINT",FACE,{"disambiguationData":[TD([[makeQuery(id+"F44.imprint","IMPRINT",EDGE,{"derivedFrom":sQuery(id+"F44.wireOp",EDGE,"E234.bottom")}),-1.0]])]});
            var Q1;
            Q1=makeQuery(id+"F44.imprint","IMPRINT",FACE,{"disambiguationData":[TD([[makeQuery(id+"F44.imprint","IMPRINT",EDGE,{"derivedFrom":sQuery(id+"F44.wireOp",EDGE,"E239.bottom")}),-1.0]])]});
            var Q2;
            Q2=makeQuery(id+"F44.imprint","IMPRINT",FACE,{"disambiguationData":[TD([[makeQuery(id+"F44.imprint","IMPRINT",EDGE,{"derivedFrom":sQuery(id+"F44.wireOp",EDGE,"E226.bottom")}),-1.0]])]});
            var Q3;
            Q3=makeQuery(id+"F44.imprint","IMPRINT",FACE,{"disambiguationData":[TD([[makeQuery(id+"F44.imprint","IMPRINT",EDGE,{"derivedFrom":sQuery(id+"F44.wireOp",EDGE,"E221.bottom")}),-1.0]])]});
            var Q4;
            {var subQ0=sQuery(id+"F1.wireOp",EDGE,"E6.rect.top");var subQ5=sQuery(id+"F7.wireOp",EDGE,"E29.left");var subQ6=makeQuery(id+"F8.opExtrude","SWEPT_FACE",FACE,{"disambiguationData":[OSD([subQ5])]});Q4=makeQuery(id+"F12.boolean.opBoolean","SPLIT",FACE,{"disambiguationData":[TD([subQ6])],"derivedFrom":makeQuery(id+"F8.boolean.opBoolean","SPLIT",FACE,{"disambiguationData":[TD([subQ6])],"derivedFrom":makeQuery(id+"F2.opExtrude","SWEPT_FACE",FACE,{"disambiguationData":[OSD([subQ0])]})})});}
            extrude(context, id + "F45", {"entities" : qUnion([Q0, Q1, Q2, Q3]), "operationType" : NewBodyOperationType.ADD, "endBound" : BoundingType.UP_TO_SURFACE, "endBoundEntityFace" : qUnion([Q4]), "depth" : 25 * mm});
        }
        {
            var Q0;
            Q0=makeQuery(id+"F31.opExtrude","SWEPT_FACE",FACE,{"disambiguationData":[OSD([sQuery(id+"F30.wireOp",EDGE,"E113.left")])]});
            cPlane(context, id + "F46", {"entities" : qUnion([Q0]), "cplaneType" : CPlaneType.OFFSET, "offset" : 50 * mm, "width" : 150 * mm, "height" : 150 * mm});
        }
        {
            var Q0;
            Q0=qCreatedBy(id+"F46.planeOp",FACE);
            var sketch = newSketch(context, id + "F47", { "sketchPlane" : qUnion([Q0])});
            skPoint(sketch, "E256.0", {"position": v(-55, -1000) * mm});
            skPoint(sketch, "E257.0", {"position": v(1435, -950) * mm});
            skLineSegment(sketch, "E258.bottom", {"start": v(1435, -950) * mm, "end": v(-55, -950) * mm, "construction": true});
            skLineSegment(sketch, "E258.top", {"start": v(1435, -1000) * mm, "end": v(-55, -1000) * mm, "construction": true});
            skLineSegment(sketch, "E258.left", {"start": v(1435, -950) * mm, "end": v(1435, -1000) * mm, "construction": true});
            skLineSegment(sketch, "E258.right", {"start": v(-55, -950) * mm, "end": v(-55, -1000) * mm, "construction": true});
            skLineSegment(sketch, "E259.0", {"start": v(665, -200) * mm, "end": v(665, -1000) * mm, "construction": true});
            skLineSegment(sketch, "E260.0", {"start": v(715, -200) * mm, "end": v(715, -1000) * mm, "construction": true});
            skPoint(sketch, "E261.orphan", {"position": v(665, -950) * mm});
            skPoint(sketch, "E262.orphan", {"position": v(715, -950) * mm});
            skLineSegment(sketch, "E263.bottom", {"start": v(670, -950) * mm, "end": v(710, -950) * mm});
            skLineSegment(sketch, "E263.top", {"start": v(670, -1000) * mm, "end": v(710, -1000) * mm});
            skLineSegment(sketch, "E263.left", {"start": v(665, -955) * mm, "end": v(665, -995) * mm});
            skLineSegment(sketch, "E263.right", {"start": v(715, -955) * mm, "end": v(715, -995) * mm});
            skArc(sketch, "E264.filletArc", {"start": v(670, -950) * mm, "mid": v(666.46, -951.46) * mm, "end": v(665, -955) * mm});
            skArc(sketch, "E265.filletArc", {"start": v(715, -955) * mm, "mid": v(713.54, -951.46) * mm, "end": v(710, -950) * mm});
            skPoint(sketch, "E266.visualSharp", {"position": v(715, -1000) * mm});
            skArc(sketch, "E266.filletArc", {"start": v(710, -1000) * mm, "mid": v(713.54, -998.54) * mm, "end": v(715, -995) * mm});
            skPoint(sketch, "E267.visualSharp", {"position": v(665, -1000) * mm});
            skArc(sketch, "E267.filletArc", {"start": v(665, -995) * mm, "mid": v(666.46, -998.54) * mm, "end": v(670, -1000) * mm});
            skSolve(sketch);
        }
        {
            var Q0;
            Q0=qSketchRegion(id+"F47",true);
            var Q1;
            Q1=makeQuery(id+"F34.boolean.opBoolean","MERGE",FACE,{"derivedFrom":[makeQuery(id+"F29.opExtrude","SWEPT_FACE",FACE,{"disambiguationData":[OSD([sQuery(id+"F28.wireOp",EDGE,"E106.left")])]}),makeQuery(id+"F34.opExtrude","SWEPT_FACE",FACE,{"disambiguationData":[OSD([sQuery(id+"F33.wireOp",EDGE,"E122.top")])]})]});
            extrude(context, id + "F48", {"entities" : qUnion([Q0]), "operationType" : NewBodyOperationType.ADD, "endBound" : BoundingType.UP_TO_NEXT, "endBoundEntity" : qUnion([Q1]), "depth" : 25 * mm, "hasSecondDirection" : true, "secondDirectionBound" : SecondDirectionBoundingType.UP_TO_NEXT, "secondDirectionOppositeDirection" : true, "secondDirectionDepth" : 25 * mm});
        }
    });
